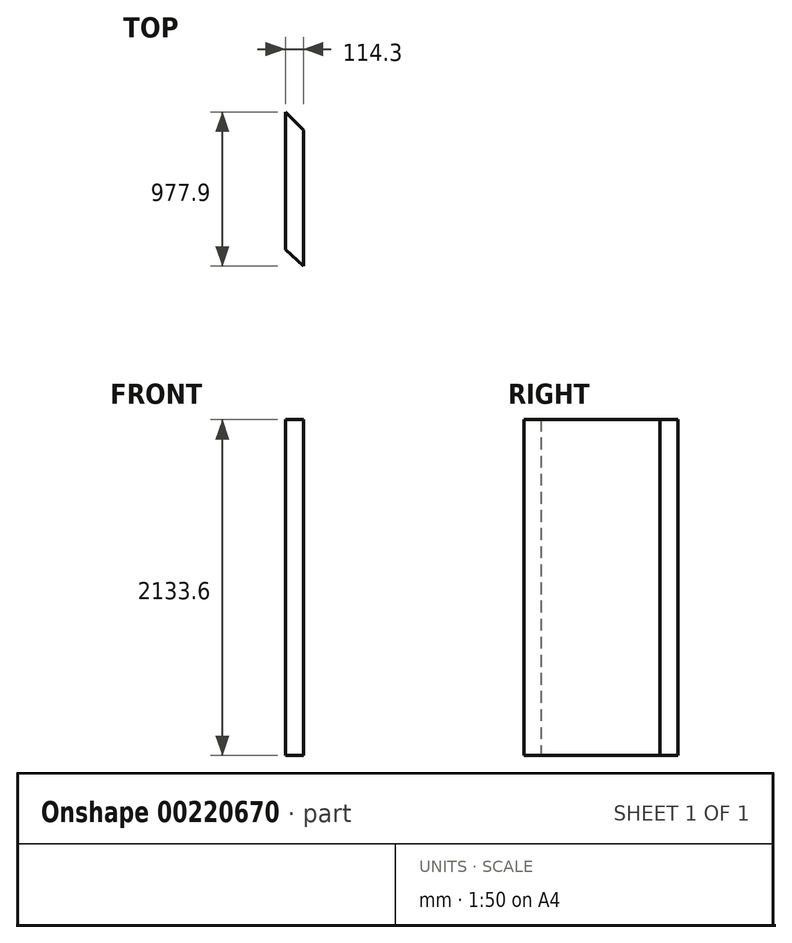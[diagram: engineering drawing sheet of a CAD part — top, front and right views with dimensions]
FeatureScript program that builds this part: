
annotation { "Feature Type Name" : "Feature", "Feature Type Description" : "" }
export const myFeature = defineFeature(function(context is Context, id is Id, definition is map)
    precondition{}
    {
        {
            var Q0;
            Q0=qCreatedBy(makeId("Top.planeOp"),FACE);
            var sketch = newSketch(context, id + "F0", { "sketchPlane" : qUnion([Q0])});
            skLineSegment(sketch, "E0.bottom", {"start": v(57.15, -431.8) * mm, "end": v(-57.15, -431.8) * mm});
            skLineSegment(sketch, "E0.top", {"start": v(57.15, 431.8) * mm, "end": v(-57.15, 431.8) * mm});
            skLineSegment(sketch, "E0.left", {"start": v(57.15, -431.8) * mm, "end": v(57.15, 431.8) * mm});
            skLineSegment(sketch, "E0.right", {"start": v(-57.15, -431.8) * mm, "end": v(-57.15, 431.8) * mm});
            skPoint(sketch, "E0.middle", {"position": v(0, 0) * mm});
            skLineSegment(sketch, "E1", {"start": v(57.15, -431.8) * mm, "end": v(-57.15, -326.4) * mm});
            skLineSegment(sketch, "E2", {"start": v(-57.15, 431.8) * mm, "end": v(-57.15, 546.1) * mm});
            skLineSegment(sketch, "E3", {"start": v(-57.15, 546.1) * mm, "end": v(57.15, 431.8) * mm});
            skSolve(sketch);
        }
        {
            var Q0;
            {var subQ0=sQuery(id+"F0.wireOp",EDGE,"E0.top");Q0=makeQuery(id+"F0.imprint","IMPRINT",FACE,{"disambiguationData":[TD([[makeQuery(id+"F0.imprint","IMPRINT",EDGE,{"derivedFrom":subQ0}),1.0]])]});}
            var Q1;
            Q1=makeQuery(id+"F0.imprint","IMPRINT",FACE,{"disambiguationData":[TD([[makeQuery(id+"F0.imprint","IMPRINT",EDGE,{"derivedFrom":sQuery(id+"F0.wireOp",EDGE,"E0.top")}),-1.0]])]});
            extrude(context, id + "F1", {"entities" : qUnion([Q0, Q1]), "endBound" : BoundingType.SYMMETRIC, "depth" : 2133.6 * mm});
        }
    });
